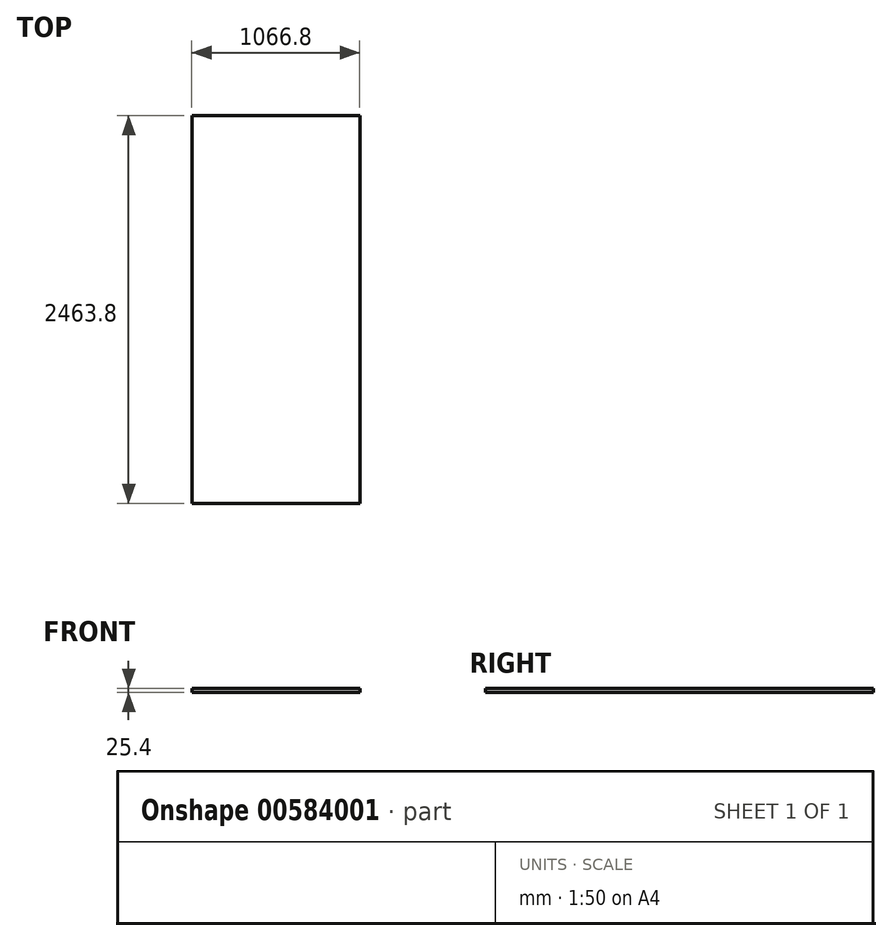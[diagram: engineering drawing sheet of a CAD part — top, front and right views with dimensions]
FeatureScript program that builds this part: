
annotation { "Feature Type Name" : "Feature", "Feature Type Description" : "" }
export const myFeature = defineFeature(function(context is Context, id is Id, definition is map)
    precondition{}
    {
        {
            var Q0;
            Q0=qCreatedBy(makeId("Top.planeOp"),FACE);
            var sketch = newSketch(context, id + "F0", { "sketchPlane" : qUnion([Q0])});
            skLineSegment(sketch, "E0.bottom", {"start": v(-535.39, 1584.48) * mm, "end": v(531.41, 1584.48) * mm});
            skLineSegment(sketch, "E0.top", {"start": v(-535.39, -879.32) * mm, "end": v(531.41, -879.32) * mm});
            skLineSegment(sketch, "E0.left", {"start": v(-535.39, 1584.48) * mm, "end": v(-535.39, -879.32) * mm});
            skLineSegment(sketch, "E0.right", {"start": v(531.41, 1584.48) * mm, "end": v(531.41, -879.32) * mm});
            skSolve(sketch);
        }
        {
            var Q0;
            Q0=makeQuery(id+"F0.imprint","IMPRINT",FACE,{"disambiguationData":[TD([[makeQuery(id+"F0.imprint","IMPRINT",EDGE,{"derivedFrom":sQuery(id+"F0.wireOp",EDGE,"E0.bottom")}),-1.0]])]});
            extrude(context, id + "F1", {"entities" : qUnion([Q0]), "depth" : 25.4 * mm, "offsetDistance" : 25.4 * mm});
        }
    });
